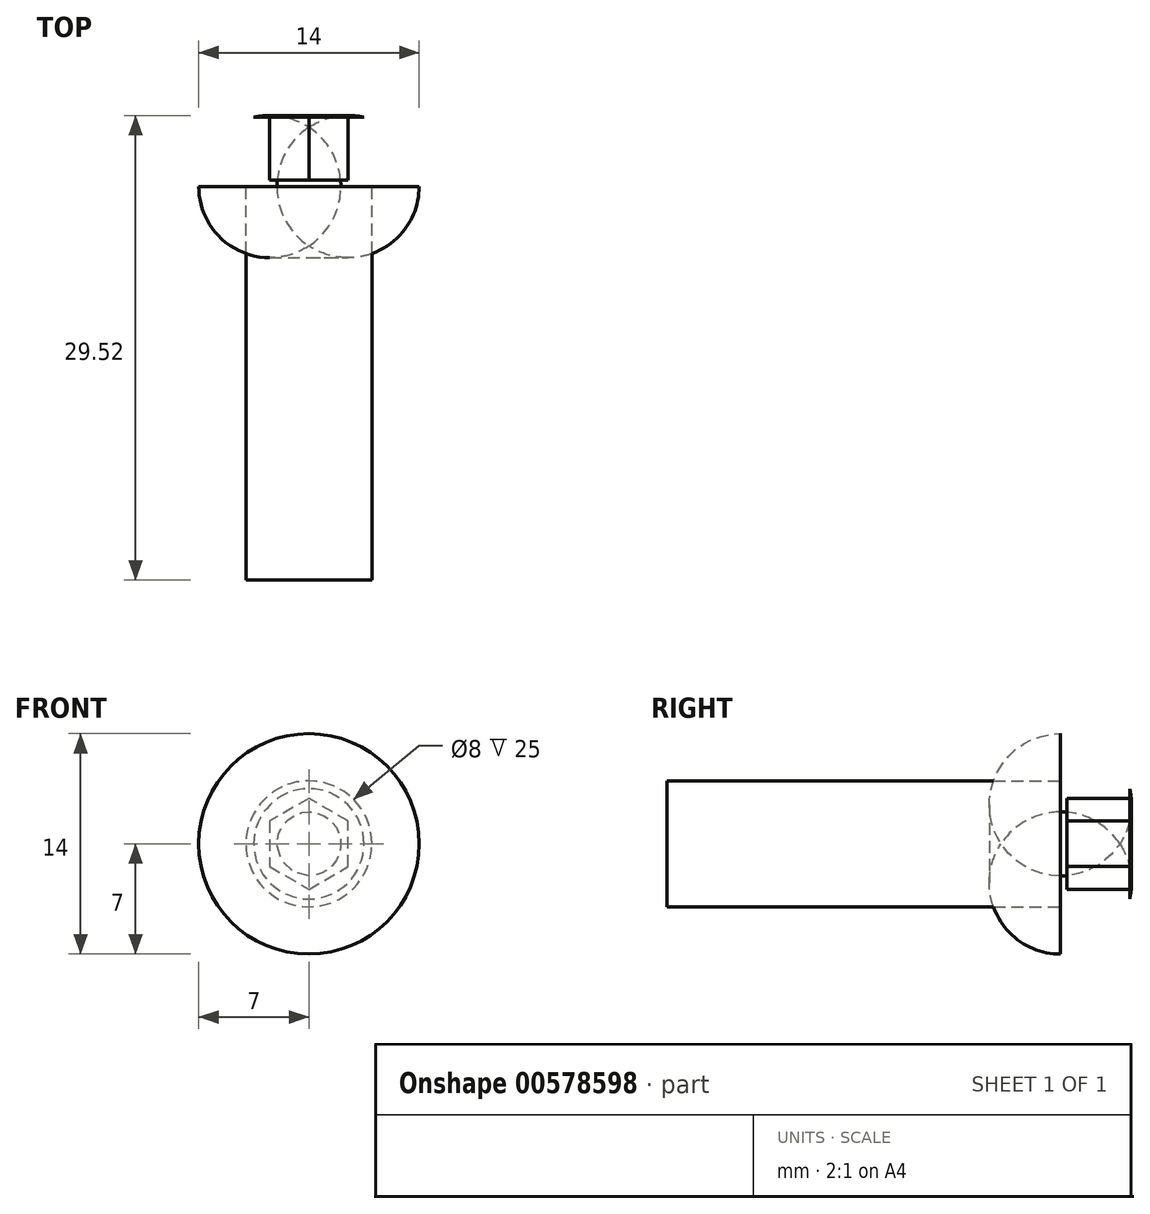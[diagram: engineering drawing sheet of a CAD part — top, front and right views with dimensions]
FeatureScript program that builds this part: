
annotation { "Feature Type Name" : "Feature", "Feature Type Description" : "" }
export const myFeature = defineFeature(function(context is Context, id is Id, definition is map)
    precondition{}
    {
        {
            var Q0;
            Q0=qCreatedBy(makeId("Front.planeOp"),FACE);
            var sketch = newSketch(context, id + "F0", { "sketchPlane" : qUnion([Q0])});
            skCircle(sketch, "E0", {"center": v(0, 0) * mm, "radius": 4 * mm});
            skSolve(sketch);
        }
        {
            var Q0;
            Q0 = qSketchRegion(id + "F0", true);
            extrude(context, id + "F1", {"entities" : qUnion([Q0]), "depth" : 25 * mm, "offsetDistance" : 25 * mm});
        }
        {
            var Q0;
            Q0=qCreatedBy(makeId("Right.planeOp"),FACE);
            var sketch = newSketch(context, id + "F2", { "sketchPlane" : qUnion([Q0])});
            skLineSegment(sketch, "E1", {"start": v(0, 0) * mm, "end": v(0, 7) * mm});
            skLineSegment(sketch, "E2", {"start": v(0, 0) * mm, "end": v(4.4, 0) * mm});
            skLineSegment(sketch, "E3", {"start": v(4.4, 0) * mm, "end": v(4.4, 2.5) * mm});
            skLineSegment(sketch, "E4", {"start": v(4.4, 2.5) * mm, "end": v(4.4, 3.5) * mm});
            skArc(sketch, "E5", {"start": v(4.4, 3.5) * mm, "mid": v(2.81, 6.02) * mm, "end": v(0, 7) * mm});
            skSolve(sketch);
        }
        {
            var Q0;
            Q0 = qSketchRegion(id + "F2", true);
            var Q1;
            Q1=makeQuery(id+"F1.opExtrude","CAP_EDGE",EDGE,{"disambiguationData":[OSD([sQuery(id+"F0.wireOp",EDGE,"E0")])],"isStart":true});
            revolve(context, id + "F3", {"operationType" : NewBodyOperationType.ADD, "entities" : qUnion([Q0]), "axis" : qUnion([Q1]), "revolveType" : RevolveType.FULL});
        }
        {
            var Q0;
            Q0=makeQuery(id+"F3.opRevolve","SWEPT_FACE",FACE,{"disambiguationData":[OSD([sQuery(id+"F2.wireOp",EDGE,"E3"),sQuery(id+"F2.wireOp",EDGE,"E4")])]});
            var sketch = newSketch(context, id + "F4", { "sketchPlane" : qUnion([Q0])});
            skCircle(sketch, "E6.cCircle", {"center": v(0, 0) * mm, "radius": 2.5 * mm, "construction": true});
            skLineSegment(sketch, "E6.0", {"start": v(-2.5, -1.44) * mm, "end": v(-2.5, 1.44) * mm});
            skLineSegment(sketch, "E6.1", {"start": v(-2.5, 1.44) * mm, "end": v(0, 2.89) * mm});
            skLineSegment(sketch, "E6.2", {"start": v(0, 2.89) * mm, "end": v(2.5, 1.44) * mm});
            skLineSegment(sketch, "E6.3", {"start": v(2.5, 1.44) * mm, "end": v(2.5, -1.44) * mm});
            skLineSegment(sketch, "E6.4", {"start": v(2.5, -1.44) * mm, "end": v(0, -2.89) * mm});
            skLineSegment(sketch, "E6.5", {"start": v(0, -2.89) * mm, "end": v(-2.5, -1.44) * mm});
            skPoint(sketch, "E6.0.midPoint", {"position": v(-2.5, 0) * mm});
            skSolve(sketch);
        }
        {
            var Q0;
            Q0 = qSketchRegion(id + "F4", true);
            extrude(context, id + "F5", {"entities" : qUnion([Q0]), "operationType" : NewBodyOperationType.REMOVE, "oppositeDirection" : true, "depth" : 4 * mm, "offsetDistance" : 25 * mm});
        }
    });
